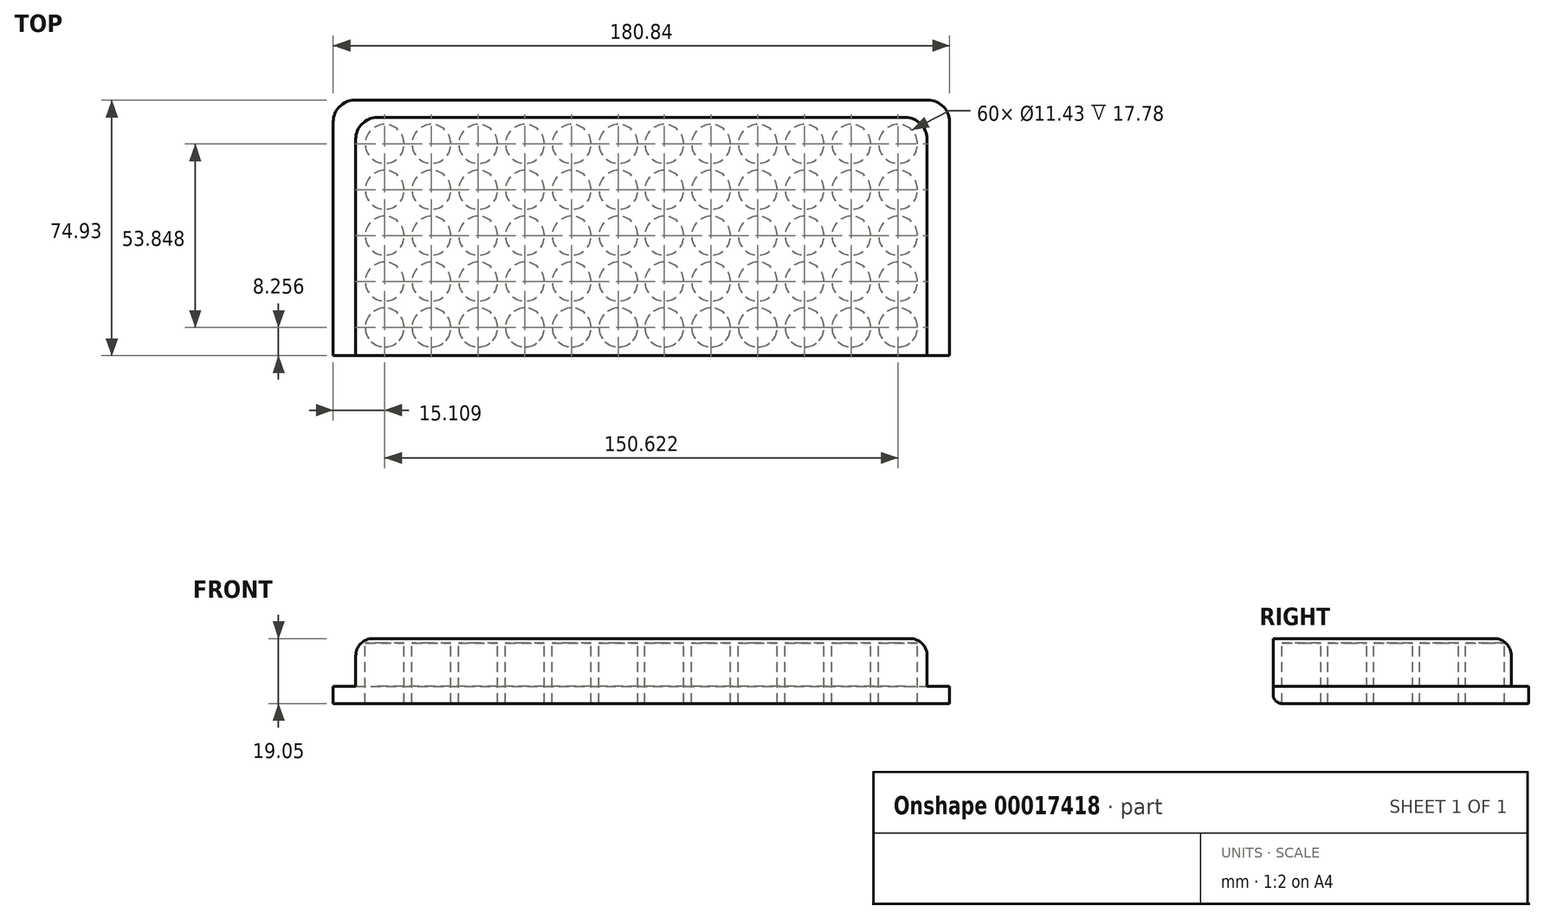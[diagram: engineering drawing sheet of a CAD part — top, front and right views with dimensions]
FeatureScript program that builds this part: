
annotation { "Feature Type Name" : "Feature", "Feature Type Description" : "" }
export const myFeature = defineFeature(function(context is Context, id is Id, definition is map)
    precondition{}
    {
        {
            var Q0;
            Q0=qCreatedBy(makeId("Top.planeOp"),FACE);
            var sketch = newSketch(context, id + "F0", { "sketchPlane" : qUnion([Q0])});
            skLineSegment(sketch, "E0.bottom", {"start": v(-83.82, -35.18) * mm, "end": v(83.82, -35.18) * mm});
            skLineSegment(sketch, "E0.top", {"start": v(-83.82, 34.67) * mm, "end": v(83.82, 34.67) * mm});
            skLineSegment(sketch, "E0.right", {"start": v(83.82, -35.18) * mm, "end": v(83.82, 34.67) * mm});
            skPoint(sketch, "E1", {"position": v(-83.31, 26.92) * mm});
            skPoint(sketch, "E2", {"position": v(-83.82, 13.46) * mm});
            skPoint(sketch, "E3", {"position": v(-83.82, 0) * mm});
            skPoint(sketch, "E4", {"position": v(-83.82, -13.46) * mm});
            skPoint(sketch, "E5", {"position": v(-83.82, -26.92) * mm});
            skPoint(sketch, "E6", {"position": v(-75.31, 34.67) * mm});
            skPoint(sketch, "E7", {"position": v(-61.6, 34.67) * mm});
            skPoint(sketch, "E8", {"position": v(-47.88, 34.67) * mm});
            skPoint(sketch, "E9", {"position": v(-34.16, 34.67) * mm});
            skPoint(sketch, "E10", {"position": v(-20.45, 34.67) * mm});
            skPoint(sketch, "E11", {"position": v(-6.73, 34.67) * mm});
            skCircle(sketch, "E12", {"center": v(-75.31, 26.92) * mm, "radius": 5.72 * mm});
            skCircle(sketch, "E13", {"center": v(-75.31, 13.46) * mm, "radius": 5.72 * mm});
            skCircle(sketch, "E14", {"center": v(-75.31, 0) * mm, "radius": 5.72 * mm});
            skCircle(sketch, "E15", {"center": v(-75.31, -13.46) * mm, "radius": 5.72 * mm});
            skCircle(sketch, "E16", {"center": v(-75.31, -26.92) * mm, "radius": 5.72 * mm});
            skCircle(sketch, "E17", {"center": v(-61.6, -26.92) * mm, "radius": 5.72 * mm});
            skCircle(sketch, "E18", {"center": v(-61.6, -13.46) * mm, "radius": 5.72 * mm});
            skCircle(sketch, "E19", {"center": v(-61.6, 0) * mm, "radius": 5.72 * mm});
            skCircle(sketch, "E20", {"center": v(-61.6, 13.46) * mm, "radius": 5.72 * mm});
            skCircle(sketch, "E21", {"center": v(-61.6, 26.92) * mm, "radius": 5.72 * mm});
            skCircle(sketch, "E22", {"center": v(-47.88, 26.92) * mm, "radius": 5.72 * mm});
            skCircle(sketch, "E23", {"center": v(-47.88, 13.46) * mm, "radius": 5.72 * mm});
            skCircle(sketch, "E24", {"center": v(-47.88, 0) * mm, "radius": 5.72 * mm});
            skCircle(sketch, "E25", {"center": v(-47.88, -13.46) * mm, "radius": 5.72 * mm});
            skCircle(sketch, "E26", {"center": v(-47.88, -26.92) * mm, "radius": 5.72 * mm});
            skCircle(sketch, "E27", {"center": v(-34.16, 26.92) * mm, "radius": 5.72 * mm});
            skCircle(sketch, "E28", {"center": v(-34.16, 13.46) * mm, "radius": 5.72 * mm});
            skCircle(sketch, "E29", {"center": v(-34.16, 0) * mm, "radius": 5.72 * mm});
            skCircle(sketch, "E30", {"center": v(-34.16, -13.46) * mm, "radius": 5.72 * mm});
            skCircle(sketch, "E31", {"center": v(-34.16, -26.92) * mm, "radius": 5.72 * mm});
            skCircle(sketch, "E32", {"center": v(-20.45, 26.92) * mm, "radius": 5.72 * mm});
            skCircle(sketch, "E33", {"center": v(-20.45, 13.46) * mm, "radius": 5.72 * mm});
            skCircle(sketch, "E34", {"center": v(-20.45, 0) * mm, "radius": 5.72 * mm});
            skCircle(sketch, "E35", {"center": v(-20.45, -13.46) * mm, "radius": 5.72 * mm});
            skCircle(sketch, "E36", {"center": v(-20.45, -26.92) * mm, "radius": 5.72 * mm});
            skCircle(sketch, "E37", {"center": v(-6.73, 26.92) * mm, "radius": 5.72 * mm});
            skCircle(sketch, "E38", {"center": v(-6.73, 13.46) * mm, "radius": 5.72 * mm});
            skCircle(sketch, "E39", {"center": v(-6.73, 0) * mm, "radius": 5.72 * mm});
            skCircle(sketch, "E40", {"center": v(-6.73, -13.46) * mm, "radius": 5.72 * mm});
            skCircle(sketch, "E41", {"center": v(-6.73, -26.92) * mm, "radius": 5.72 * mm});
            skPoint(sketch, "E42", {"position": v(0, -35.18) * mm});
            skCircle(sketch, "E43.MirrorC", {"center": v(6.73, 26.92) * mm, "radius": 5.72 * mm});
            skCircle(sketch, "E44.MirrorC", {"center": v(47.88, 0) * mm, "radius": 5.72 * mm});
            skCircle(sketch, "E45.MirrorC", {"center": v(6.73, 0) * mm, "radius": 5.72 * mm});
            skCircle(sketch, "E46.MirrorC", {"center": v(20.45, 0) * mm, "radius": 5.72 * mm});
            skCircle(sketch, "E47.MirrorC", {"center": v(34.16, -13.46) * mm, "radius": 5.72 * mm});
            skCircle(sketch, "E48.MirrorC", {"center": v(47.88, -26.92) * mm, "radius": 5.72 * mm});
            skCircle(sketch, "E49.MirrorC", {"center": v(34.16, 26.92) * mm, "radius": 5.72 * mm});
            skCircle(sketch, "E50.MirrorC", {"center": v(20.45, 13.46) * mm, "radius": 5.72 * mm});
            skCircle(sketch, "E51.MirrorC", {"center": v(34.16, 0) * mm, "radius": 5.72 * mm});
            skCircle(sketch, "E52.MirrorC", {"center": v(6.73, -13.46) * mm, "radius": 5.72 * mm});
            skCircle(sketch, "E53.MirrorC", {"center": v(61.6, 26.92) * mm, "radius": 5.72 * mm});
            skCircle(sketch, "E54.MirrorC", {"center": v(75.31, 0) * mm, "radius": 5.72 * mm});
            skCircle(sketch, "E55.MirrorC", {"center": v(20.45, 26.92) * mm, "radius": 5.72 * mm});
            skCircle(sketch, "E56.MirrorC", {"center": v(20.45, -26.92) * mm, "radius": 5.72 * mm});
            skCircle(sketch, "E57.MirrorC", {"center": v(34.16, -26.92) * mm, "radius": 5.72 * mm});
            skCircle(sketch, "E58.MirrorC", {"center": v(34.16, 13.46) * mm, "radius": 5.72 * mm});
            skCircle(sketch, "E59.MirrorC", {"center": v(47.88, 26.92) * mm, "radius": 5.72 * mm});
            skCircle(sketch, "E60.MirrorC", {"center": v(75.31, 13.46) * mm, "radius": 5.72 * mm});
            skCircle(sketch, "E61.MirrorC", {"center": v(47.88, 13.46) * mm, "radius": 5.72 * mm});
            skCircle(sketch, "E62.MirrorC", {"center": v(61.6, -13.46) * mm, "radius": 5.72 * mm});
            skCircle(sketch, "E63.MirrorC", {"center": v(47.88, -13.46) * mm, "radius": 5.72 * mm});
            skCircle(sketch, "E64.MirrorC", {"center": v(6.73, 13.46) * mm, "radius": 5.72 * mm});
            skCircle(sketch, "E65.MirrorC", {"center": v(61.6, 0) * mm, "radius": 5.72 * mm});
            skCircle(sketch, "E66.MirrorC", {"center": v(20.45, -13.46) * mm, "radius": 5.72 * mm});
            skCircle(sketch, "E67.MirrorC", {"center": v(61.6, 13.46) * mm, "radius": 5.72 * mm});
            skCircle(sketch, "E68.MirrorC", {"center": v(61.6, -26.92) * mm, "radius": 5.72 * mm});
            skCircle(sketch, "E69.MirrorC", {"center": v(75.31, -26.92) * mm, "radius": 5.72 * mm});
            skCircle(sketch, "E70.MirrorC", {"center": v(75.31, 26.92) * mm, "radius": 5.72 * mm});
            skCircle(sketch, "E71.MirrorC", {"center": v(6.73, -26.92) * mm, "radius": 5.72 * mm});
            skCircle(sketch, "E72.MirrorC", {"center": v(75.31, -13.46) * mm, "radius": 5.72 * mm});
            skLineSegment(sketch, "E73", {"start": v(-83.82, 34.67) * mm, "end": v(-83.82, -35.18) * mm});
            skSolve(sketch);
        }
        {
            var Q0;
            Q0=makeQuery(id+"F0.imprint","IMPRINT",FACE,{"disambiguationData":[TD([[makeQuery(id+"F0.imprint","IMPRINT",EDGE,{"derivedFrom":sQuery(id+"F0.wireOp",EDGE,"E0.bottom")}),1.0]])]});
            extrude(context, id + "F1", {"entities" : qUnion([Q0]), "depth" : 19.05 * mm});
        }
        {
            var Q0;
            Q0=qCreatedBy(makeId("Top.planeOp"),FACE);
            var sketch = newSketch(context, id + "F2", { "sketchPlane" : qUnion([Q0])});
            skLineSegment(sketch, "E74.bottom", {"start": v(83.82, 34.67) * mm, "end": v(-83.82, 34.67) * mm});
            skLineSegment(sketch, "E74.top", {"start": v(83.82, -35.18) * mm, "end": v(-83.82, -35.18) * mm});
            skLineSegment(sketch, "E74.left", {"start": v(83.82, 34.67) * mm, "end": v(83.82, -35.18) * mm});
            skLineSegment(sketch, "E74.right", {"start": v(-83.82, 34.67) * mm, "end": v(-83.82, -35.18) * mm});
            skSolve(sketch);
        }
        {
            var Q0;
            Q0 = qSketchRegion(id + "F2", true);
            extrude(context, id + "F3", {"entities" : qUnion([Q0]), "operationType" : NewBodyOperationType.ADD, "depth" : 1.27 * mm});
        }
        {
            var Q0;
            Q0=makeQuery(id+"F1.opExtrude","CAP_FACE",FACE,{"disambiguationData":[OSD([sQuery(id+"F0.wireOp",EDGE,"E0.bottom"),sQuery(id+"F0.wireOp",EDGE,"E0.top"),sQuery(id+"F0.wireOp",EDGE,"E0.left"),sQuery(id+"F0.wireOp",EDGE,"E0.right"),sQuery(id+"F0.wireOp",EDGE,"E12"),sQuery(id+"F0.wireOp",EDGE,"E13"),sQuery(id+"F0.wireOp",EDGE,"E14"),sQuery(id+"F0.wireOp",EDGE,"E15"),sQuery(id+"F0.wireOp",EDGE,"E16"),sQuery(id+"F0.wireOp",EDGE,"E17"),sQuery(id+"F0.wireOp",EDGE,"E18"),sQuery(id+"F0.wireOp",EDGE,"E19"),sQuery(id+"F0.wireOp",EDGE,"E20"),sQuery(id+"F0.wireOp",EDGE,"E21"),sQuery(id+"F0.wireOp",EDGE,"E22"),sQuery(id+"F0.wireOp",EDGE,"E23"),sQuery(id+"F0.wireOp",EDGE,"E24"),sQuery(id+"F0.wireOp",EDGE,"E25"),sQuery(id+"F0.wireOp",EDGE,"E26"),sQuery(id+"F0.wireOp",EDGE,"E27"),sQuery(id+"F0.wireOp",EDGE,"E28"),sQuery(id+"F0.wireOp",EDGE,"E29"),sQuery(id+"F0.wireOp",EDGE,"E30"),sQuery(id+"F0.wireOp",EDGE,"E31"),sQuery(id+"F0.wireOp",EDGE,"E32"),sQuery(id+"F0.wireOp",EDGE,"E33"),sQuery(id+"F0.wireOp",EDGE,"E34"),sQuery(id+"F0.wireOp",EDGE,"E35"),sQuery(id+"F0.wireOp",EDGE,"E36"),sQuery(id+"F0.wireOp",EDGE,"E37"),sQuery(id+"F0.wireOp",EDGE,"E38"),sQuery(id+"F0.wireOp",EDGE,"E39"),sQuery(id+"F0.wireOp",EDGE,"E40"),sQuery(id+"F0.wireOp",EDGE,"E41"),sQuery(id+"F0.wireOp",EDGE,"E43.MirrorC"),sQuery(id+"F0.wireOp",EDGE,"E44.MirrorC"),sQuery(id+"F0.wireOp",EDGE,"E45.MirrorC"),sQuery(id+"F0.wireOp",EDGE,"E46.MirrorC"),sQuery(id+"F0.wireOp",EDGE,"E47.MirrorC"),sQuery(id+"F0.wireOp",EDGE,"E48.MirrorC"),sQuery(id+"F0.wireOp",EDGE,"E49.MirrorC"),sQuery(id+"F0.wireOp",EDGE,"E50.MirrorC"),sQuery(id+"F0.wireOp",EDGE,"E51.MirrorC"),sQuery(id+"F0.wireOp",EDGE,"E52.MirrorC"),sQuery(id+"F0.wireOp",EDGE,"E53.MirrorC"),sQuery(id+"F0.wireOp",EDGE,"E54.MirrorC"),sQuery(id+"F0.wireOp",EDGE,"E55.MirrorC"),sQuery(id+"F0.wireOp",EDGE,"E56.MirrorC"),sQuery(id+"F0.wireOp",EDGE,"E57.MirrorC"),sQuery(id+"F0.wireOp",EDGE,"E58.MirrorC"),sQuery(id+"F0.wireOp",EDGE,"E59.MirrorC"),sQuery(id+"F0.wireOp",EDGE,"E60.MirrorC"),sQuery(id+"F0.wireOp",EDGE,"E61.MirrorC"),sQuery(id+"F0.wireOp",EDGE,"E62.MirrorC"),sQuery(id+"F0.wireOp",EDGE,"E63.MirrorC"),sQuery(id+"F0.wireOp",EDGE,"E64.MirrorC"),sQuery(id+"F0.wireOp",EDGE,"E65.MirrorC"),sQuery(id+"F0.wireOp",EDGE,"E66.MirrorC"),sQuery(id+"F0.wireOp",EDGE,"E67.MirrorC"),sQuery(id+"F0.wireOp",EDGE,"E68.MirrorC"),sQuery(id+"F0.wireOp",EDGE,"E69.MirrorC"),sQuery(id+"F0.wireOp",EDGE,"E70.MirrorC"),sQuery(id+"F0.wireOp",EDGE,"E71.MirrorC"),sQuery(id+"F0.wireOp",EDGE,"E72.MirrorC")])],"isStart":false});
            var sketch = newSketch(context, id + "F4", { "sketchPlane" : qUnion([Q0])});
            skLineSegment(sketch, "E75", {"start": v(-83.82, -35.18) * mm, "end": v(-83.82, 34.67) * mm});
            skLineSegment(sketch, "E76", {"start": v(-83.82, 34.67) * mm, "end": v(83.82, 34.67) * mm});
            skLineSegment(sketch, "E77", {"start": v(83.82, 34.67) * mm, "end": v(83.82, -35.18) * mm});
            skLineSegment(sketch, "E78", {"start": v(83.82, -35.18) * mm, "end": v(90.42, -35.18) * mm});
            skLineSegment(sketch, "E79", {"start": v(90.42, -35.18) * mm, "end": v(90.42, 39.75) * mm});
            skLineSegment(sketch, "E80", {"start": v(90.42, 39.75) * mm, "end": v(-90.42, 39.75) * mm});
            skLineSegment(sketch, "E81", {"start": v(-90.42, 39.75) * mm, "end": v(-90.42, -35.18) * mm});
            skLineSegment(sketch, "E82", {"start": v(-90.42, -35.18) * mm, "end": v(-83.82, -35.18) * mm});
            skSolve(sketch);
        }
        {
            var Q0;
            Q0 = qSketchRegion(id + "F4", true);
            extrude(context, id + "F5", {"entities" : qUnion([Q0]), "operationType" : NewBodyOperationType.ADD, "oppositeDirection" : true, "depth" : 5.08 * mm});
        }
        {
            var Q0;
            Q0=makeQuery(id+"F1.opExtrude","SWEPT_EDGE",EDGE,{"disambiguationData":[OSD([sQuery(id+"F0.wireOp",EDGE,"E0.top"),sQuery(id+"F0.wireOp",EDGE,"E73")])]});
            var Q1;
            Q1=makeQuery(id+"F5.opExtrude","SWEPT_EDGE",EDGE,{"disambiguationData":[OSD([sQuery(id+"F4.wireOp",EDGE,"E79"),sQuery(id+"F4.wireOp",EDGE,"E80")])]});
            var Q2;
            Q2=makeQuery(id+"F5.opExtrude","SWEPT_EDGE",EDGE,{"disambiguationData":[OSD([sQuery(id+"F4.wireOp",EDGE,"E80"),sQuery(id+"F4.wireOp",EDGE,"E81")])]});
            var Q3;
            Q3=makeQuery(id+"F1.opExtrude","SWEPT_EDGE",EDGE,{"disambiguationData":[OSD([sQuery(id+"F0.wireOp",EDGE,"E0.top"),sQuery(id+"F0.wireOp",EDGE,"E0.right")])]});
            fillet(context, id + "F6", {"entities" : qUnion([Q0, Q1, Q2, Q3]), "radius" : 6.35 * mm, "tangentPropagation" : true, "allowEdgeOverflow" : false});
        }
        {
            var Q0;
            Q0=qCreatedBy(makeId("Right.planeOp"),FACE);
            var sketch = newSketch(context, id + "F7", { "sketchPlane" : qUnion([Q0])});
            skLineSegment(sketch, "E83", {"start": v(-35.18, 0) * mm, "end": v(-35.18, 19.05) * mm});
            skPoint(sketch, "E84", {"position": v(-35.18, 9.53) * mm});
            skSolve(sketch);
        }
        {
            var Q0;
            Q0=qCreatedBy(makeId("Right.planeOp"),FACE);
            var sketch = newSketch(context, id + "F8", { "sketchPlane" : qUnion([Q0])});
            skLineSegment(sketch, "E85", {"start": v(-35.18, 9.53) * mm, "end": v(85.15, 9.53) * mm});
            skSolve(sketch);
        }
        {
            var Q0;
            Q0=makeQuery(id+"F1.opExtrude","SWEPT_BODY",BODY,{"disambiguationData":[OSD([sQuery(id+"F0.wireOp",EDGE,"E0.bottom"),sQuery(id+"F0.wireOp",EDGE,"E0.top"),sQuery(id+"F0.wireOp",EDGE,"E0.left"),sQuery(id+"F0.wireOp",EDGE,"E0.right"),sQuery(id+"F0.wireOp",EDGE,"E12"),sQuery(id+"F0.wireOp",EDGE,"E13"),sQuery(id+"F0.wireOp",EDGE,"E14"),sQuery(id+"F0.wireOp",EDGE,"E15"),sQuery(id+"F0.wireOp",EDGE,"E16"),sQuery(id+"F0.wireOp",EDGE,"E17"),sQuery(id+"F0.wireOp",EDGE,"E18"),sQuery(id+"F0.wireOp",EDGE,"E19"),sQuery(id+"F0.wireOp",EDGE,"E20"),sQuery(id+"F0.wireOp",EDGE,"E21"),sQuery(id+"F0.wireOp",EDGE,"E22"),sQuery(id+"F0.wireOp",EDGE,"E23"),sQuery(id+"F0.wireOp",EDGE,"E24"),sQuery(id+"F0.wireOp",EDGE,"E25"),sQuery(id+"F0.wireOp",EDGE,"E26"),sQuery(id+"F0.wireOp",EDGE,"E27"),sQuery(id+"F0.wireOp",EDGE,"E28"),sQuery(id+"F0.wireOp",EDGE,"E29"),sQuery(id+"F0.wireOp",EDGE,"E30"),sQuery(id+"F0.wireOp",EDGE,"E31"),sQuery(id+"F0.wireOp",EDGE,"E32"),sQuery(id+"F0.wireOp",EDGE,"E33"),sQuery(id+"F0.wireOp",EDGE,"E34"),sQuery(id+"F0.wireOp",EDGE,"E35"),sQuery(id+"F0.wireOp",EDGE,"E36"),sQuery(id+"F0.wireOp",EDGE,"E37"),sQuery(id+"F0.wireOp",EDGE,"E38"),sQuery(id+"F0.wireOp",EDGE,"E39"),sQuery(id+"F0.wireOp",EDGE,"E40"),sQuery(id+"F0.wireOp",EDGE,"E41"),sQuery(id+"F0.wireOp",EDGE,"E43.MirrorC"),sQuery(id+"F0.wireOp",EDGE,"E44.MirrorC"),sQuery(id+"F0.wireOp",EDGE,"E45.MirrorC"),sQuery(id+"F0.wireOp",EDGE,"E46.MirrorC"),sQuery(id+"F0.wireOp",EDGE,"E47.MirrorC"),sQuery(id+"F0.wireOp",EDGE,"E48.MirrorC"),sQuery(id+"F0.wireOp",EDGE,"E49.MirrorC"),sQuery(id+"F0.wireOp",EDGE,"E50.MirrorC"),sQuery(id+"F0.wireOp",EDGE,"E51.MirrorC"),sQuery(id+"F0.wireOp",EDGE,"E52.MirrorC"),sQuery(id+"F0.wireOp",EDGE,"E53.MirrorC"),sQuery(id+"F0.wireOp",EDGE,"E54.MirrorC"),sQuery(id+"F0.wireOp",EDGE,"E55.MirrorC"),sQuery(id+"F0.wireOp",EDGE,"E56.MirrorC"),sQuery(id+"F0.wireOp",EDGE,"E57.MirrorC"),sQuery(id+"F0.wireOp",EDGE,"E58.MirrorC"),sQuery(id+"F0.wireOp",EDGE,"E59.MirrorC"),sQuery(id+"F0.wireOp",EDGE,"E60.MirrorC"),sQuery(id+"F0.wireOp",EDGE,"E61.MirrorC"),sQuery(id+"F0.wireOp",EDGE,"E62.MirrorC"),sQuery(id+"F0.wireOp",EDGE,"E63.MirrorC"),sQuery(id+"F0.wireOp",EDGE,"E64.MirrorC"),sQuery(id+"F0.wireOp",EDGE,"E65.MirrorC"),sQuery(id+"F0.wireOp",EDGE,"E66.MirrorC"),sQuery(id+"F0.wireOp",EDGE,"E67.MirrorC"),sQuery(id+"F0.wireOp",EDGE,"E68.MirrorC"),sQuery(id+"F0.wireOp",EDGE,"E69.MirrorC"),sQuery(id+"F0.wireOp",EDGE,"E70.MirrorC"),sQuery(id+"F0.wireOp",EDGE,"E71.MirrorC"),sQuery(id+"F0.wireOp",EDGE,"E72.MirrorC")])]});
            var Q1;
            Q1=sQuery(id+"F8.wireOp",EDGE,"E85");
            transform(context, id + "F9", {"entities" : qUnion([Q0]), "transformType" : TransformType.ROTATION, "transformAxis" : qUnion([Q1]), "angle" : 180 * degree, "makeCopy" : false});
        }
        {
            var Q0;
            Q0=makeQuery(id+"F5.boolean.opBoolean","MERGE",EDGE,{"derivedFrom":[makeQuery(id+"F1.opExtrude","CAP_EDGE",EDGE,{"disambiguationData":[OSD([sQuery(id+"F0.wireOp",EDGE,"E0.bottom")])],"isStart":false}),makeQuery(id+"F5.opExtrude","CAP_EDGE",EDGE,{"disambiguationData":[OSD([sQuery(id+"F4.wireOp",EDGE,"E78")])],"isStart":true}),makeQuery(id+"F5.opExtrude","CAP_EDGE",EDGE,{"disambiguationData":[OSD([sQuery(id+"F4.wireOp",EDGE,"E82")])],"isStart":true})]});
            fillet(context, id + "F10", {"entities" : qUnion([Q0]), "radius" : 2.54 * mm, "tangentPropagation" : true, "allowEdgeOverflow" : false});
        }
        {
            var Q0;
            Q0=makeQuery(id+"F1.opExtrude","CAP_EDGE",EDGE,{"disambiguationData":[OSD([sQuery(id+"F0.wireOp",EDGE,"E73")])],"isStart":true});
            var Q1;
            Q1=makeQuery(id+"F5.opExtrude","CAP_EDGE",EDGE,{"disambiguationData":[OSD([sQuery(id+"F4.wireOp",EDGE,"E75")])],"isStart":false});
            fillet(context, id + "F11", {"entities" : qUnion([Q0, Q1]), "radius" : 5.08 * mm, "tangentPropagation" : true, "allowEdgeOverflow" : false});
        }
    });
